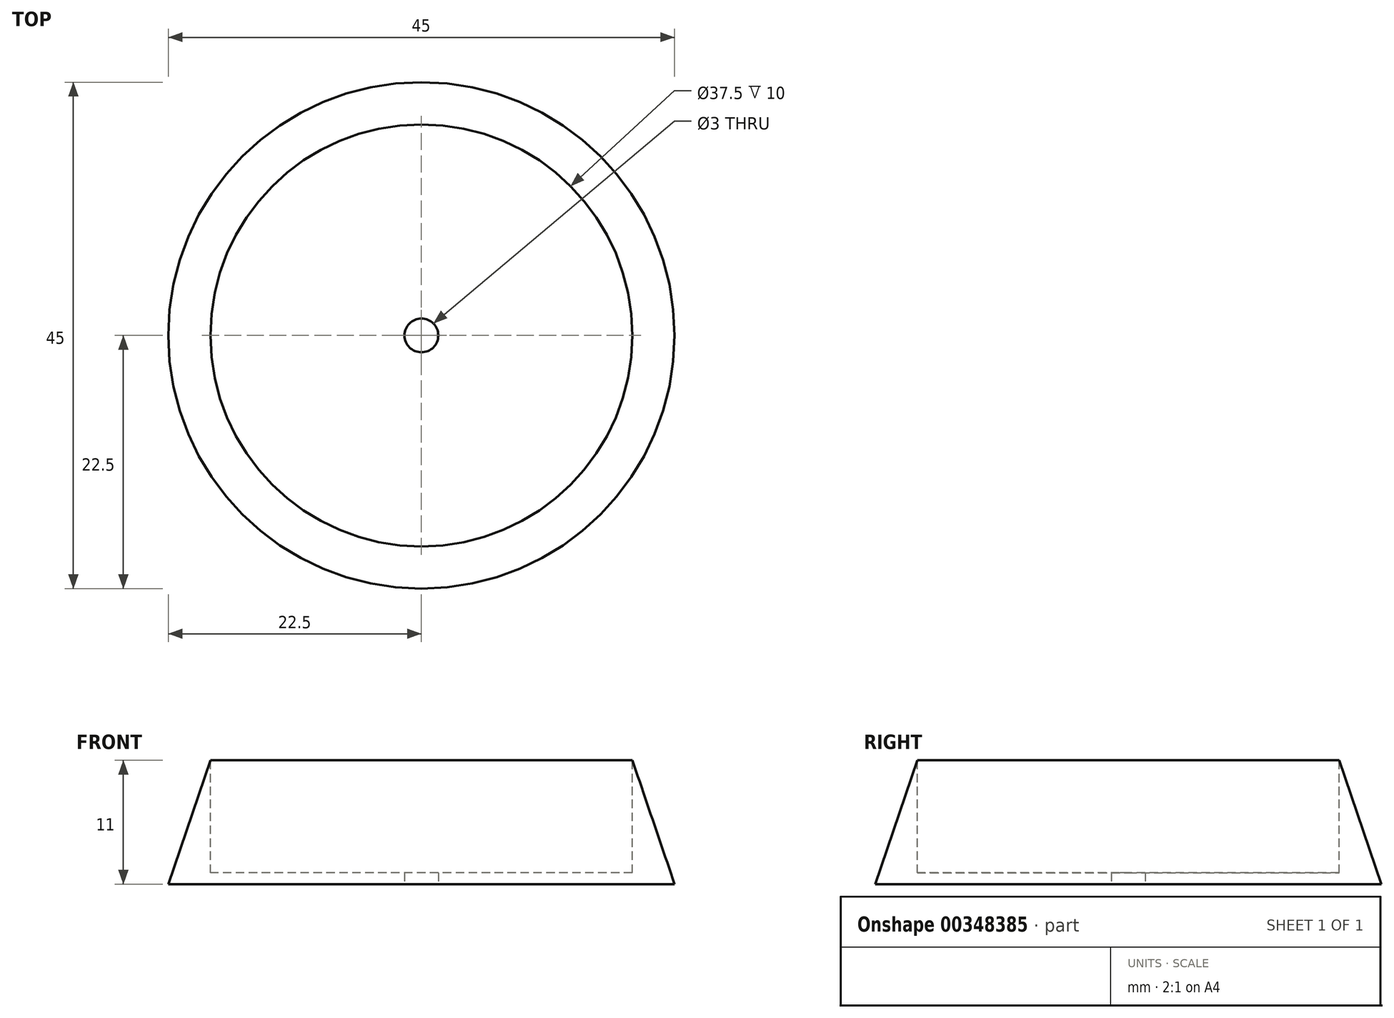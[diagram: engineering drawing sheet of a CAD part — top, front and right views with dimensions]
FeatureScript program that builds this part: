
annotation { "Feature Type Name" : "Feature", "Feature Type Description" : "" }
export const myFeature = defineFeature(function(context is Context, id is Id, definition is map)
    precondition{}
    {
        {
            var Q0;
            Q0=qCreatedBy(makeId("Top.planeOp"),FACE);
            var sketch = newSketch(context, id + "F0", { "sketchPlane" : qUnion([Q0])});
            skCircle(sketch, "E0", {"center": v(0, 0) * mm, "radius": 22.5 * mm});
            skLineSegment(sketch, "E1", {"start": v(0, 0) * mm, "end": v(0, 22.5) * mm});
            skSolve(sketch);
        }
        {
            assignVariable(context, id + "F1", {"name" : "firstPartHeight", "anyValue" : 11});
        }
        {
            var Q0;
            Q0=qCreatedBy(makeId("Top.planeOp"),FACE);
            cPlane(context, id + "F2", {"entities" : qUnion([Q0]), "cplaneType" : CPlaneType.OFFSET, "offset" : (getVariable(context, 'firstPartHeight')) * mm, "width" : 150 * mm, "height" : 150 * mm});
        }
        {
            var Q0;
            Q0=qCreatedBy(id+"F2.planeOp",FACE);
            var sketch = newSketch(context, id + "F3", { "sketchPlane" : qUnion([Q0])});
            skCircle(sketch, "E2", {"center": v(0, 0) * mm, "radius": 18.75 * mm});
            skLineSegment(sketch, "E3", {"start": v(0, 0) * mm, "end": v(0, 18.75) * mm});
            skSolve(sketch);
        }
        {
            var Q0;
            {var subQ0=sQuery(id+"F0.wireOp",EDGE,"E0");Q0=makeQuery(id+"F0.imprint","IMPRINT",FACE,{"disambiguationData":[TD([[makeQuery(id+"F0.imprint","IMPRINT",EDGE,{"disambiguationData":[TD([[makeQuery(id+"F0.imprint","IMPRINT",VERTEX,{"derivedFrom":subQ0}),-1.0]])],"derivedFrom":subQ0}),1.0]])]});}
            var Q1;
            {var subQ0=sQuery(id+"F3.wireOp",EDGE,"E2");Q1=makeQuery(id+"F3.imprint","IMPRINT",FACE,{"disambiguationData":[TD([[makeQuery(id+"F3.imprint","IMPRINT",EDGE,{"disambiguationData":[TD([[makeQuery(id+"F3.imprint","IMPRINT",VERTEX,{"derivedFrom":subQ0}),-1.0]])],"derivedFrom":subQ0}),1.0]])]});}
            loft(context, id + "F4", {"sheetProfilesArray" : [{ "sheetProfileEntities" : qUnion([Q0]) }, { "sheetProfileEntities" : qUnion([Q1]) }]});
        }
        {
            var Q0;
            {var subQ0=sQuery(id+"F3.wireOp",EDGE,"E2");Q0=makeQuery(id+"F4.opLoft","CAP_FACE",FACE,{"disambiguationData":[OSD([makeQuery(id+"F3.imprint","IMPRINT",FACE,{"disambiguationData":[TD([[makeQuery(id+"F3.imprint","IMPRINT",EDGE,{"disambiguationData":[TD([[makeQuery(id+"F3.imprint","IMPRINT",VERTEX,{"derivedFrom":subQ0}),-1.0]])],"derivedFrom":subQ0}),1.0]])]})])],"isStart":true});}
            extrude(context, id + "F5", {"entities" : qUnion([Q0]), "operationType" : NewBodyOperationType.REMOVE, "oppositeDirection" : true, "depth" : (getVariable(context, 'firstPartHeight') - 1) * mm});
        }
        {
            var Q0;
            {var subQ0=sQuery(id+"F0.wireOp",EDGE,"E0");Q0=makeQuery(id+"F4.opLoft","CAP_FACE",FACE,{"disambiguationData":[OSD([makeQuery(id+"F0.imprint","IMPRINT",FACE,{"disambiguationData":[TD([[makeQuery(id+"F0.imprint","IMPRINT",EDGE,{"disambiguationData":[TD([[makeQuery(id+"F0.imprint","IMPRINT",VERTEX,{"derivedFrom":subQ0}),-1.0]])],"derivedFrom":subQ0}),1.0]])]})])],"isStart":true});}
            var sketch = newSketch(context, id + "F6", { "sketchPlane" : qUnion([Q0])});
            skCircle(sketch, "E4", {"center": v(0, 0) * mm, "radius": 1.5 * mm});
            skSolve(sketch);
        }
        {
            var Q0;
            Q0=makeQuery(id+"F6.imprint","IMPRINT",FACE,{"disambiguationData":[TD([[makeQuery(id+"F6.imprint","IMPRINT",EDGE,{"derivedFrom":sQuery(id+"F6.wireOp",EDGE,"E4")}),1.0]])]});
            extrude(context, id + "F7", {"entities" : qUnion([Q0]), "operationType" : NewBodyOperationType.REMOVE, "endBound" : BoundingType.UP_TO_NEXT, "oppositeDirection" : true, "depth" : 25 * mm});
        }
    });
